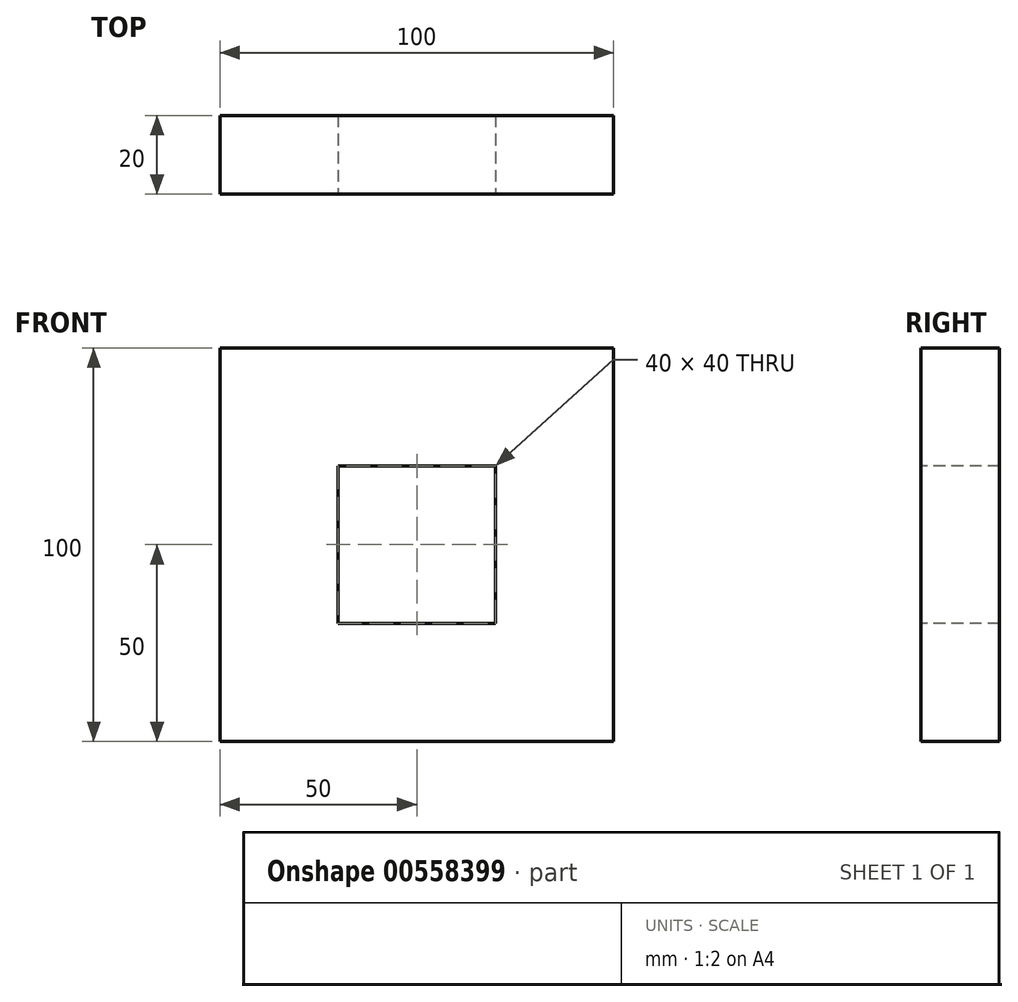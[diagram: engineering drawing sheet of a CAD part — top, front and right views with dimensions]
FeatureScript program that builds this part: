
annotation { "Feature Type Name" : "Feature", "Feature Type Description" : "" }
export const myFeature = defineFeature(function(context is Context, id is Id, definition is map)
    precondition{}
    {
        {
            var Q0;
            Q0=qCreatedBy(makeId("Front.planeOp"),FACE);
            var sketch = newSketch(context, id + "F0", { "sketchPlane" : qUnion([Q0])});
            skLineSegment(sketch, "E0.bottom", {"start": v(50, 50) * mm, "end": v(-50, 50) * mm});
            skLineSegment(sketch, "E0.top", {"start": v(50, -50) * mm, "end": v(-50, -50) * mm});
            skLineSegment(sketch, "E0.left", {"start": v(50, 50) * mm, "end": v(50, -50) * mm});
            skLineSegment(sketch, "E0.right", {"start": v(-50, 50) * mm, "end": v(-50, -50) * mm});
            skPoint(sketch, "E0.middle", {"position": v(0, 0) * mm});
            skSolve(sketch);
        }
        {
            var Q0;
            Q0 = qSketchRegion(id + "F0", true);
            extrude(context, id + "F1", {"entities" : qUnion([Q0]), "depth" : 20 * mm, "offsetDistance" : 25 * mm});
        }
        {
            var Q0;
            Q0=makeQuery(id+"F1.opExtrude","CAP_FACE",FACE,{"disambiguationData":[OSD([sQuery(id+"F0.wireOp",EDGE,"E0.bottom"),sQuery(id+"F0.wireOp",EDGE,"E0.top"),sQuery(id+"F0.wireOp",EDGE,"E0.left"),sQuery(id+"F0.wireOp",EDGE,"E0.right")])],"isStart":false});
            var sketch = newSketch(context, id + "F2", { "sketchPlane" : qUnion([Q0])});
            skLineSegment(sketch, "E1.bottom", {"start": v(20, 20) * mm, "end": v(-20, 20) * mm});
            skLineSegment(sketch, "E1.top", {"start": v(20, -20) * mm, "end": v(-20, -20) * mm});
            skLineSegment(sketch, "E1.left", {"start": v(20, 20) * mm, "end": v(20, -20) * mm});
            skLineSegment(sketch, "E1.right", {"start": v(-20, 20) * mm, "end": v(-20, -20) * mm});
            skPoint(sketch, "E1.middle", {"position": v(0, 0) * mm});
            skSolve(sketch);
        }
        {
            var Q0;
            Q0=makeQuery(id+"F2.imprint","IMPRINT",FACE,{"disambiguationData":[TD([[makeQuery(id+"F2.imprint","IMPRINT",EDGE,{"derivedFrom":sQuery(id+"F2.wireOp",EDGE,"E1.bottom")}),1.0]])]});
            extrude(context, id + "F3", {"entities" : qUnion([Q0]), "operationType" : NewBodyOperationType.REMOVE, "oppositeDirection" : true, "depth" : 20 * mm, "offsetDistance" : 25 * mm});
        }
    });
